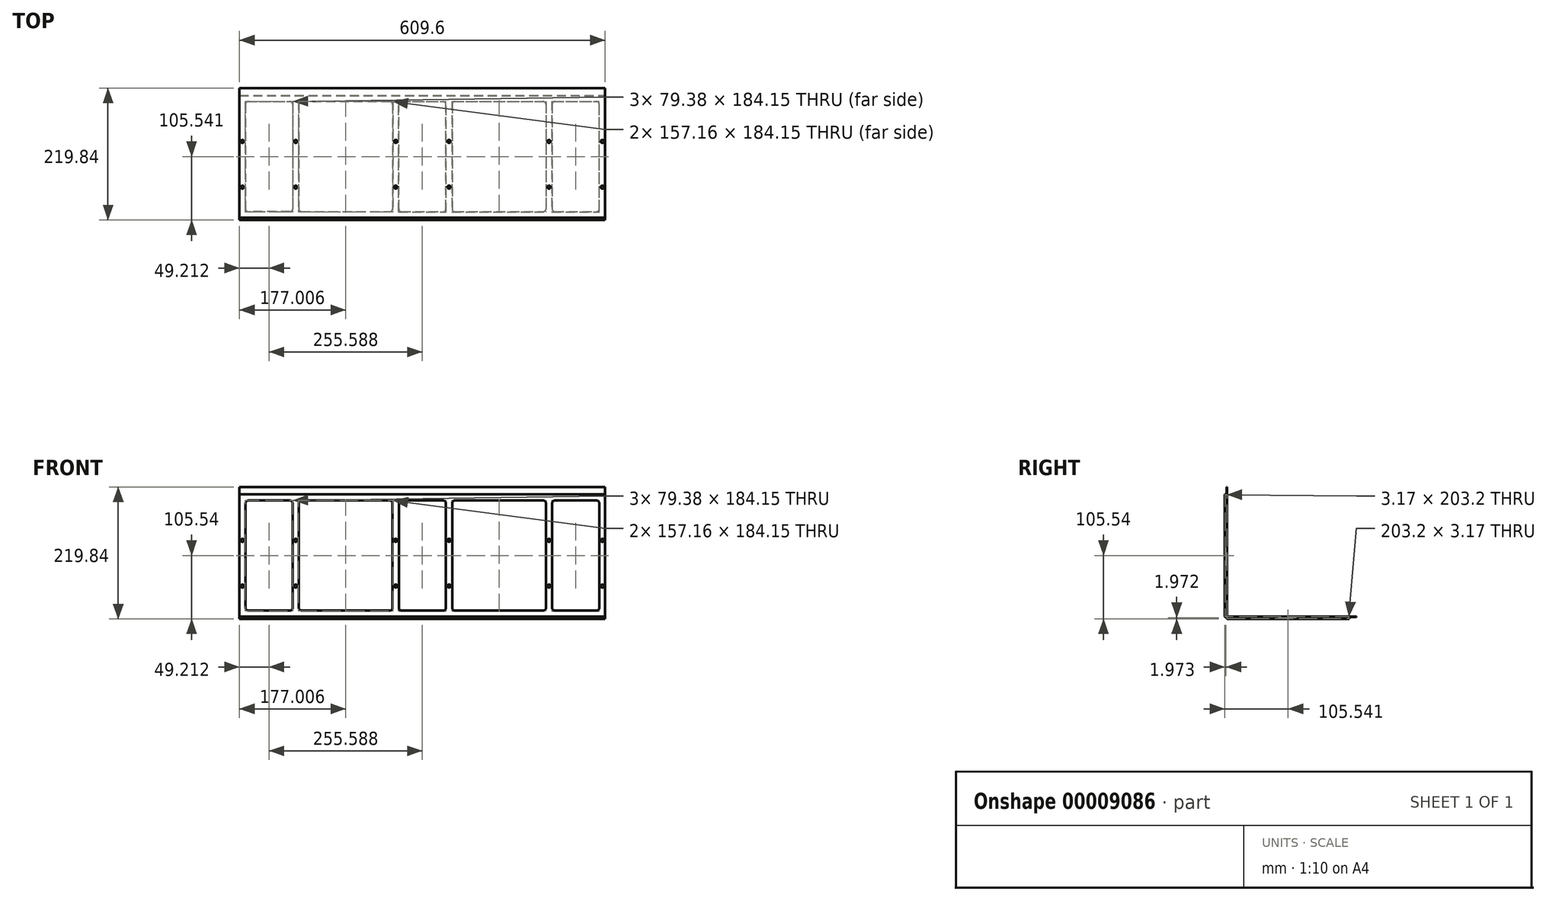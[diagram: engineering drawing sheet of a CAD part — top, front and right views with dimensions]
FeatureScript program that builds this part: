
annotation { "Feature Type Name" : "Feature", "Feature Type Description" : "" }
export const myFeature = defineFeature(function(context is Context, id is Id, definition is map)
    precondition{}
    {
        {
            var Q0;
            Q0=qCreatedBy(makeId("Front.planeOp"),FACE);
            var sketch = newSketch(context, id + "F0", { "sketchPlane" : qUnion([Q0])});
            skLineSegment(sketch, "E0.bottom", {"start": v(0, 0) * mm, "end": v(609.6, 0) * mm});
            skLineSegment(sketch, "E0.top", {"start": v(0, 203.2) * mm, "end": v(609.6, 203.2) * mm});
            skLineSegment(sketch, "E0.left", {"start": v(0, 0) * mm, "end": v(0, 203.2) * mm});
            skLineSegment(sketch, "E0.right", {"start": v(609.6, 0) * mm, "end": v(609.6, 203.2) * mm});
            skLineSegment(sketch, "E1.left", {"start": v(9.52, 193.68) * mm, "end": v(9.53, 9.52) * mm});
            skLineSegment(sketch, "E2.right", {"start": v(600.08, 9.53) * mm, "end": v(600.08, 193.68) * mm});
            skPoint(sketch, "E3", {"position": v(304.8, 203.2) * mm});
            skPoint(sketch, "E4", {"position": v(304.8, 0) * mm});
            skLineSegment(sketch, "E5.bottom", {"start": v(354.01, 193.68) * mm, "end": v(511.18, 193.68) * mm});
            skLineSegment(sketch, "E5.top", {"start": v(354.01, 9.53) * mm, "end": v(511.18, 9.53) * mm});
            skCircle(sketch, "E6", {"center": v(4.76, 127) * mm, "radius": 2.54 * mm});
            skCircle(sketch, "E7", {"center": v(4.76, 50.8) * mm, "radius": 2.54 * mm});
            skCircle(sketch, "E8", {"center": v(604.84, 127) * mm, "radius": 2.54 * mm});
            skCircle(sketch, "E9", {"center": v(604.84, 50.8) * mm, "radius": 2.54 * mm});
            skLineSegment(sketch, "E10.bottom", {"start": v(88.9, 193.68) * mm, "end": v(98.42, 193.68) * mm, "construction": true});
            skLineSegment(sketch, "E10.top", {"start": v(88.9, 9.52) * mm, "end": v(98.43, 9.52) * mm, "construction": true});
            skLineSegment(sketch, "E10.left", {"start": v(88.9, 193.68) * mm, "end": v(88.9, 9.53) * mm});
            skLineSegment(sketch, "E10.right", {"start": v(98.43, 193.68) * mm, "end": v(98.43, 9.53) * mm});
            skPoint(sketch, "E11", {"position": v(93.66, 193.68) * mm});
            skPoint(sketch, "E12", {"position": v(93.66, 127) * mm});
            skPoint(sketch, "E13", {"position": v(93.66, 50.8) * mm});
            skLineSegment(sketch, "E14", {"start": v(265.11, 9.53) * mm, "end": v(265.11, 193.68) * mm});
            skLineSegment(sketch, "E15", {"start": v(265.11, 193.68) * mm, "end": v(255.59, 193.68) * mm, "construction": true});
            skLineSegment(sketch, "E16", {"start": v(255.59, 193.68) * mm, "end": v(255.59, 9.53) * mm});
            skLineSegment(sketch, "E17", {"start": v(344.49, 9.53) * mm, "end": v(344.49, 193.67) * mm});
            skLineSegment(sketch, "E18", {"start": v(344.49, 193.68) * mm, "end": v(354.01, 193.68) * mm, "construction": true});
            skLineSegment(sketch, "E19", {"start": v(354.01, 193.68) * mm, "end": v(354.01, 9.53) * mm});
            skLineSegment(sketch, "E20.trimOffspring", {"start": v(265.11, 193.68) * mm, "end": v(344.49, 193.68) * mm});
            skPoint(sketch, "E21", {"position": v(260.35, 193.68) * mm});
            skPoint(sketch, "E22", {"position": v(349.25, 193.68) * mm});
            skCircle(sketch, "E23", {"center": v(93.66, 127) * mm, "radius": 2.54 * mm});
            skCircle(sketch, "E24", {"center": v(93.66, 50.8) * mm, "radius": 2.54 * mm});
            skCircle(sketch, "E25", {"center": v(260.35, 50.8) * mm, "radius": 2.54 * mm});
            skCircle(sketch, "E26", {"center": v(260.35, 127) * mm, "radius": 2.54 * mm});
            skCircle(sketch, "E27", {"center": v(349.25, 127) * mm, "radius": 2.54 * mm});
            skCircle(sketch, "E28", {"center": v(349.25, 50.8) * mm, "radius": 2.54 * mm});
            skLineSegment(sketch, "E29.trimOffspring", {"start": v(265.11, 9.53) * mm, "end": v(344.49, 9.53) * mm});
            skLineSegment(sketch, "E30.bottom", {"start": v(520.7, 193.68) * mm, "end": v(511.18, 193.68) * mm, "construction": true});
            skLineSegment(sketch, "E30.left", {"start": v(511.18, 193.68) * mm, "end": v(511.18, 9.53) * mm});
            skLineSegment(sketch, "E30.right", {"start": v(520.7, 193.68) * mm, "end": v(520.7, 9.53) * mm});
            skLineSegment(sketch, "E31.trimOffspring", {"start": v(520.7, 9.53) * mm, "end": v(600.08, 9.53) * mm});
            skLineSegment(sketch, "E32.trimOffspring", {"start": v(520.7, 193.68) * mm, "end": v(600.08, 193.68) * mm});
            skCircle(sketch, "E33", {"center": v(515.94, 127) * mm, "radius": 2.54 * mm});
            skCircle(sketch, "E34", {"center": v(515.94, 50.8) * mm, "radius": 2.54 * mm});
            skPoint(sketch, "E35", {"position": v(515.94, 193.67) * mm});
            skLineSegment(sketch, "E36", {"start": v(515.94, 193.67) * mm, "end": v(515.94, 9.53) * mm, "construction": true});
            skLineSegment(sketch, "E37", {"start": v(354.01, 9.53) * mm, "end": v(600.08, 9.53) * mm, "construction": true});
            skLineSegment(sketch, "E38", {"start": v(98.42, 193.68) * mm, "end": v(255.59, 193.68) * mm});
            skLineSegment(sketch, "E39", {"start": v(255.59, 9.53) * mm, "end": v(98.43, 9.52) * mm});
            skLineSegment(sketch, "E40", {"start": v(88.9, 9.53) * mm, "end": v(9.53, 9.52) * mm});
            skLineSegment(sketch, "E41", {"start": v(9.52, 193.68) * mm, "end": v(88.9, 193.68) * mm});
            skPoint(sketch, "E42", {"position": v(304.8, 9.53) * mm});
            skSolve(sketch);
        }
        {
            var Q0;
            Q0=makeQuery(id+"F0.imprint","IMPRINT",FACE,{"disambiguationData":[TD([[makeQuery(id+"F0.imprint","IMPRINT",EDGE,{"derivedFrom":sQuery(id+"F0.wireOp",EDGE,"E0.bottom")}),1.0]])]});
            extrude(context, id + "F1", {"entities" : qUnion([Q0]), "depth" : 3.17 * mm});
        }
        {
            var Q0;
            Q0=makeQuery(id+"F1.opExtrude","SWEPT_FACE",FACE,{"disambiguationData":[OSD([sQuery(id+"F0.wireOp",EDGE,"E0.right")])]});
            var sketch = newSketch(context, id + "F2", { "sketchPlane" : qUnion([Q0])});
            skLineSegment(sketch, "E43.0.0", {"start": v(0, 0) * mm, "end": v(0, 203.2) * mm});
            skLineSegment(sketch, "E43.0.1", {"start": v(0, 203.2) * mm, "end": v(-3.18, 203.2) * mm});
            skLineSegment(sketch, "E43.0.2", {"start": v(-3.18, 203.2) * mm, "end": v(-3.18, 0) * mm});
            skLineSegment(sketch, "E43.0.3", {"start": v(-3.18, 0) * mm, "end": v(0, 0) * mm});
            skLineSegment(sketch, "E44.0", {"start": v(0.38, 0) * mm, "end": v(0.38, 203.2) * mm});
            skLineSegment(sketch, "E45.0", {"start": v(-3.56, 203.2) * mm, "end": v(-3.56, 0) * mm});
            skLineSegment(sketch, "E46", {"start": v(-3.18, 203.2) * mm, "end": v(0, 203.2) * mm});
            skLineSegment(sketch, "E47", {"start": v(-3.56, 0) * mm, "end": v(0.38, 0) * mm});
            skLineSegment(sketch, "E48", {"start": v(0.38, 203.2) * mm, "end": v(0.38, 215.9) * mm});
            skLineSegment(sketch, "E49", {"start": v(0.38, 215.9) * mm, "end": v(-0.38, 215.9) * mm});
            skLineSegment(sketch, "E50", {"start": v(-0.38, 215.9) * mm, "end": v(-0.38, 204.85) * mm});
            skLineSegment(sketch, "E51", {"start": v(-3.56, 203.2) * mm, "end": v(-3.56, 203.58) * mm});
            skLineSegment(sketch, "E52", {"start": v(-3.56, 203.58) * mm, "end": v(-1.65, 203.58) * mm});
            skPoint(sketch, "E53.visualSharp", {"position": v(-0.38, 203.58) * mm});
            skArc(sketch, "E53.filletArc", {"start": v(-1.65, 203.58) * mm, "mid": v(-0.75, 203.95) * mm, "end": v(-0.38, 204.85) * mm});
            skLineSegment(sketch, "E54", {"start": v(0.38, 0) * mm, "end": v(-1.52, -1.9) * mm});
            skLineSegment(sketch, "E55", {"start": v(-3.56, 0) * mm, "end": v(-3.56, -0.38) * mm});
            skArc(sketch, "E56", {"start": v(-1.52, -1.9) * mm, "mid": v(-2.48, -1.07) * mm, "end": v(-3.56, -0.38) * mm});
            skLineSegment(sketch, "E57", {"start": v(-1.83, -1.6) * mm, "end": v(-1.52, -1.9) * mm, "construction": true});
            skSolve(sketch);
        }
        {
            var Q0;
            {var subQ2=sQuery(id+"F2.wireOp",EDGE,"E43.0.0");Q0=makeQuery(id+"F2.imprint","IMPRINT",FACE,{"disambiguationData":[TD([[makeQuery(id+"F2.imprint","IMPRINT",EDGE,{"derivedFrom":subQ2}),1.0]])]});}
            var Q1;
            {var subQ1=sQuery(id+"F2.wireOp",EDGE,"E54");Q1=makeQuery(id+"F2.imprint","IMPRINT",FACE,{"disambiguationData":[TD([[makeQuery(id+"F2.imprint","IMPRINT",EDGE,{"derivedFrom":subQ1}),-1.0]])]});}
            var Q2;
            {var subQ2=sQuery(id+"F2.wireOp",EDGE,"E43.0.0");Q2=makeQuery(id+"F2.imprint","IMPRINT",FACE,{"disambiguationData":[TD([[makeQuery(id+"F2.imprint","IMPRINT",EDGE,{"derivedFrom":subQ2}),-1.0]])]});}
            var Q3;
            Q3=makeQuery(id+"F1.opExtrude","SWEPT_FACE",FACE,{"disambiguationData":[OSD([sQuery(id+"F0.wireOp",EDGE,"E0.left")])]});
            extrude(context, id + "F3", {"entities" : qUnion([Q0, Q1, Q2]), "endBound" : BoundingType.UP_TO_SURFACE, "oppositeDirection" : true, "endBoundEntityFace" : qUnion([Q3]), "depth" : 25.4 * mm});
        }
        {
            var Q0;
            Q0=makeQuery(id+"F0.imprint","IMPRINT",FACE,{"disambiguationData":[TD([[makeQuery(id+"F0.imprint","IMPRINT",EDGE,{"derivedFrom":sQuery(id+"F0.wireOp",EDGE,"E0.bottom")}),1.0]])]});
            var Q1;
            Q1=makeQuery(id+"F0.imprint","IMPRINT",FACE,{"disambiguationData":[TD([[makeQuery(id+"F0.imprint","IMPRINT",EDGE,{"derivedFrom":sQuery(id+"F0.wireOp",EDGE,"e5c9517b-3403-446c-b804-9a1888062617")}),1.0]])]});
            var Q2;
            Q2=makeQuery(id+"F0.imprint","IMPRINT",FACE,{"disambiguationData":[TD([[makeQuery(id+"F0.imprint","IMPRINT",EDGE,{"derivedFrom":sQuery(id+"F0.wireOp",EDGE,"d61da92c-88b1-4440-b826-febfc96da58b")}),1.0]])]});
            var Q3;
            Q3=makeQuery(id+"F0.imprint","IMPRINT",FACE,{"disambiguationData":[TD([[makeQuery(id+"F0.imprint","IMPRINT",EDGE,{"derivedFrom":sQuery(id+"F0.wireOp",EDGE,"46ce25ad-17ab-4da1-9f69-b3d8d2fa4a44")}),1.0]])]});
            var Q4;
            Q4=makeQuery(id+"F0.imprint","IMPRINT",FACE,{"disambiguationData":[TD([[makeQuery(id+"F0.imprint","IMPRINT",EDGE,{"derivedFrom":sQuery(id+"F0.wireOp",EDGE,"ffe5e0e1-37b3-4eca-acac-06d890d8a48e")}),1.0]])]});
            var Q5;
            Q5=makeQuery(id+"F0.imprint","IMPRINT",FACE,{"disambiguationData":[TD([[makeQuery(id+"F0.imprint","IMPRINT",EDGE,{"derivedFrom":sQuery(id+"F0.wireOp",EDGE,"E9")}),1.0]])]});
            var Q6;
            Q6=makeQuery(id+"F0.imprint","IMPRINT",FACE,{"disambiguationData":[TD([[makeQuery(id+"F0.imprint","IMPRINT",EDGE,{"derivedFrom":sQuery(id+"F0.wireOp",EDGE,"E8")}),1.0]])]});
            var Q7;
            Q7=makeQuery(id+"F0.imprint","IMPRINT",FACE,{"disambiguationData":[TD([[makeQuery(id+"F0.imprint","IMPRINT",EDGE,{"derivedFrom":sQuery(id+"F0.wireOp",EDGE,"8ca14061-9922-471c-a98a-c78a47010712")}),1.0]])]});
            var Q8;
            Q8=makeQuery(id+"F0.imprint","IMPRINT",FACE,{"disambiguationData":[TD([[makeQuery(id+"F0.imprint","IMPRINT",EDGE,{"derivedFrom":sQuery(id+"F0.wireOp",EDGE,"fd383d34-7c74-4bab-aac5-eb13519cfafe")}),1.0]])]});
            var Q9;
            Q9=makeQuery(id+"F0.imprint","IMPRINT",FACE,{"disambiguationData":[TD([[makeQuery(id+"F0.imprint","IMPRINT",EDGE,{"derivedFrom":sQuery(id+"F0.wireOp",EDGE,"E7")}),1.0]])]});
            var Q10;
            Q10=makeQuery(id+"F0.imprint","IMPRINT",FACE,{"disambiguationData":[TD([[makeQuery(id+"F0.imprint","IMPRINT",EDGE,{"derivedFrom":sQuery(id+"F0.wireOp",EDGE,"E6")}),1.0]])]});
            var Q11;
            Q11=makeQuery(id+"F3.opExtrude","SWEPT_FACE",FACE,{"disambiguationData":[OSD([sQuery(id+"F2.wireOp",EDGE,"E45.0"),sQuery(id+"F2.wireOp",EDGE,"E51"),sQuery(id+"F2.wireOp",EDGE,"E55")])]});
            extrude(context, id + "F4", {"entities" : qUnion([Q0, Q1, Q2, Q3, Q4, Q5, Q6, Q7, Q8, Q9, Q10, Q11]), "operationType" : NewBodyOperationType.REMOVE, "depth" : 3.17 * mm});
        }
        {
            var Q0;
            Q0=makeQuery(id+"F0.imprint","IMPRINT",FACE,{"disambiguationData":[TD([[makeQuery(id+"F0.imprint","IMPRINT",EDGE,{"derivedFrom":sQuery(id+"F0.wireOp",EDGE,"8ca14061-9922-471c-a98a-c78a47010712")}),1.0]])]});
            var Q1;
            Q1=makeQuery(id+"F0.imprint","IMPRINT",FACE,{"disambiguationData":[TD([[makeQuery(id+"F0.imprint","IMPRINT",EDGE,{"derivedFrom":sQuery(id+"F0.wireOp",EDGE,"fd383d34-7c74-4bab-aac5-eb13519cfafe")}),1.0]])]});
            var Q2;
            Q2=makeQuery(id+"F0.imprint","IMPRINT",FACE,{"disambiguationData":[TD([[makeQuery(id+"F0.imprint","IMPRINT",EDGE,{"derivedFrom":sQuery(id+"F0.wireOp",EDGE,"E7")}),1.0]])]});
            var Q3;
            Q3=makeQuery(id+"F0.imprint","IMPRINT",FACE,{"disambiguationData":[TD([[makeQuery(id+"F0.imprint","IMPRINT",EDGE,{"derivedFrom":sQuery(id+"F0.wireOp",EDGE,"E6")}),1.0]])]});
            var Q4;
            Q4=makeQuery(id+"F0.imprint","IMPRINT",FACE,{"disambiguationData":[TD([[makeQuery(id+"F0.imprint","IMPRINT",EDGE,{"derivedFrom":sQuery(id+"F0.wireOp",EDGE,"d61da92c-88b1-4440-b826-febfc96da58b")}),1.0]])]});
            var Q5;
            Q5=makeQuery(id+"F0.imprint","IMPRINT",FACE,{"disambiguationData":[TD([[makeQuery(id+"F0.imprint","IMPRINT",EDGE,{"derivedFrom":sQuery(id+"F0.wireOp",EDGE,"e5c9517b-3403-446c-b804-9a1888062617")}),1.0]])]});
            var Q6;
            Q6=makeQuery(id+"F0.imprint","IMPRINT",FACE,{"disambiguationData":[TD([[makeQuery(id+"F0.imprint","IMPRINT",EDGE,{"derivedFrom":sQuery(id+"F0.wireOp",EDGE,"ffe5e0e1-37b3-4eca-acac-06d890d8a48e")}),1.0]])]});
            var Q7;
            Q7=makeQuery(id+"F0.imprint","IMPRINT",FACE,{"disambiguationData":[TD([[makeQuery(id+"F0.imprint","IMPRINT",EDGE,{"derivedFrom":sQuery(id+"F0.wireOp",EDGE,"46ce25ad-17ab-4da1-9f69-b3d8d2fa4a44")}),1.0]])]});
            var Q8;
            Q8=makeQuery(id+"F0.imprint","IMPRINT",FACE,{"disambiguationData":[TD([[makeQuery(id+"F0.imprint","IMPRINT",EDGE,{"derivedFrom":sQuery(id+"F0.wireOp",EDGE,"E9")}),1.0]])]});
            var Q9;
            Q9=makeQuery(id+"F0.imprint","IMPRINT",FACE,{"disambiguationData":[TD([[makeQuery(id+"F0.imprint","IMPRINT",EDGE,{"derivedFrom":sQuery(id+"F0.wireOp",EDGE,"E8")}),1.0]])]});
            var Q10;
            Q10=makeQuery(id+"F0.imprint","IMPRINT",FACE,{"disambiguationData":[TD([[makeQuery(id+"F0.imprint","IMPRINT",EDGE,{"derivedFrom":sQuery(id+"F0.wireOp",EDGE,"E26")}),1.0]])]});
            var Q11;
            Q11=makeQuery(id+"F0.imprint","IMPRINT",FACE,{"disambiguationData":[TD([[makeQuery(id+"F0.imprint","IMPRINT",EDGE,{"derivedFrom":sQuery(id+"F0.wireOp",EDGE,"E25")}),1.0]])]});
            var Q12;
            Q12=makeQuery(id+"F0.imprint","IMPRINT",FACE,{"disambiguationData":[TD([[makeQuery(id+"F0.imprint","IMPRINT",EDGE,{"derivedFrom":sQuery(id+"F0.wireOp",EDGE,"E24")}),1.0]])]});
            var Q13;
            Q13=makeQuery(id+"F0.imprint","IMPRINT",FACE,{"disambiguationData":[TD([[makeQuery(id+"F0.imprint","IMPRINT",EDGE,{"derivedFrom":sQuery(id+"F0.wireOp",EDGE,"E23")}),1.0]])]});
            var Q14;
            Q14=makeQuery(id+"F0.imprint","IMPRINT",FACE,{"disambiguationData":[TD([[makeQuery(id+"F0.imprint","IMPRINT",EDGE,{"derivedFrom":sQuery(id+"F0.wireOp",EDGE,"E28")}),1.0]])]});
            var Q15;
            Q15=makeQuery(id+"F0.imprint","IMPRINT",FACE,{"disambiguationData":[TD([[makeQuery(id+"F0.imprint","IMPRINT",EDGE,{"derivedFrom":sQuery(id+"F0.wireOp",EDGE,"E27")}),1.0]])]});
            var Q16;
            Q16=makeQuery(id+"F0.imprint","IMPRINT",FACE,{"disambiguationData":[TD([[makeQuery(id+"F0.imprint","IMPRINT",EDGE,{"derivedFrom":sQuery(id+"F0.wireOp",EDGE,"E34")}),1.0]])]});
            var Q17;
            Q17=makeQuery(id+"F0.imprint","IMPRINT",FACE,{"disambiguationData":[TD([[makeQuery(id+"F0.imprint","IMPRINT",EDGE,{"derivedFrom":sQuery(id+"F0.wireOp",EDGE,"E33")}),1.0]])]});
            extrude(context, id + "F5", {"entities" : qUnion([Q0, Q1, Q2, Q3, Q4, Q5, Q6, Q7, Q8, Q9, Q10, Q11, Q12, Q13, Q14, Q15, Q16, Q17]), "operationType" : NewBodyOperationType.REMOVE, "endBound" : BoundingType.SYMMETRIC, "depth" : 25.4 * mm});
        }
        {
            var Q0;
            Q0=makeQuery(id+"F3.opExtrude","SWEPT_FACE",FACE,{"disambiguationData":[OSD([sQuery(id+"F2.wireOp",EDGE,"E45.0"),sQuery(id+"F2.wireOp",EDGE,"E51"),sQuery(id+"F2.wireOp",EDGE,"E55")])]});
            var sketch = newSketch(context, id + "F6", { "sketchPlane" : qUnion([Q0])});
            skLineSegment(sketch, "E58.0.1", {"start": v(0, 0) * mm, "end": v(609.6, 0) * mm});
            skLineSegment(sketch, "E58.0.3", {"start": v(609.6, 203.2) * mm, "end": v(0, 203.2) * mm});
            skLineSegment(sketch, "E59.0.0", {"start": v(255.59, 193.68) * mm, "end": v(98.42, 193.68) * mm});
            skLineSegment(sketch, "E59.0.2", {"start": v(98.43, 9.52) * mm, "end": v(255.59, 9.53) * mm});
            skLineSegment(sketch, "E60.1", {"start": v(609.6, 0) * mm, "end": v(609.6, -3.18) * mm});
            skLineSegment(sketch, "E60.3", {"start": v(609.6, -3.18) * mm, "end": v(609.6, 0) * mm});
            skLineSegment(sketch, "E60.6", {"start": v(609.6, -3.18) * mm, "end": v(609.6, 0) * mm});
            skLineSegment(sketch, "E60.7", {"start": v(609.6, -3.56) * mm, "end": v(609.6, 0.38) * mm});
            skLineSegment(sketch, "E60.9", {"start": v(609.6, 0.38) * mm, "end": v(609.6, -0.38) * mm});
            skLineSegment(sketch, "E60.12", {"start": v(609.6, -3.56) * mm, "end": v(609.6, -1.65) * mm});
            skPoint(sketch, "E60.13", {"position": v(609.6, 203.58) * mm});
            skLineSegment(sketch, "E60.14", {"start": v(609.6, 204.85) * mm, "end": v(609.6, 203.58) * mm});
            skLineSegment(sketch, "E60.15", {"start": v(609.6, 0) * mm, "end": v(609.6, -1.9) * mm});
            skLineSegment(sketch, "E60.17", {"start": v(609.6, -0.38) * mm, "end": v(609.6, -1.9) * mm});
            skLineSegment(sketch, "E60.18", {"start": v(609.6, -1.6) * mm, "end": v(609.6, -1.9) * mm});
            skLineSegment(sketch, "E61.0", {"start": v(88.9, 193.68) * mm, "end": v(88.9, 9.53) * mm});
            skLineSegment(sketch, "E61.1", {"start": v(88.9, 9.53) * mm, "end": v(9.53, 9.52) * mm});
            skLineSegment(sketch, "E61.2", {"start": v(9.52, 193.68) * mm, "end": v(88.9, 193.68) * mm});
            skLineSegment(sketch, "E61.3", {"start": v(9.52, 193.68) * mm, "end": v(9.53, 9.52) * mm});
            skLineSegment(sketch, "E62.0", {"start": v(98.43, 193.68) * mm, "end": v(98.43, 9.53) * mm});
            skLineSegment(sketch, "E62.1", {"start": v(255.59, 193.68) * mm, "end": v(255.59, 9.53) * mm});
            skLineSegment(sketch, "E62.2", {"start": v(265.11, 9.53) * mm, "end": v(265.11, 193.68) * mm});
            skLineSegment(sketch, "E62.3", {"start": v(344.49, 9.53) * mm, "end": v(344.49, 193.67) * mm});
            skLineSegment(sketch, "E62.4", {"start": v(354.01, 193.68) * mm, "end": v(354.01, 9.53) * mm});
            skLineSegment(sketch, "E62.5", {"start": v(511.18, 193.68) * mm, "end": v(511.18, 9.53) * mm});
            skLineSegment(sketch, "E62.6", {"start": v(520.7, 193.68) * mm, "end": v(520.7, 9.53) * mm});
            skLineSegment(sketch, "E62.7", {"start": v(600.08, 9.53) * mm, "end": v(600.08, 193.68) * mm});
            skLineSegment(sketch, "E62.8", {"start": v(354.01, 193.68) * mm, "end": v(511.18, 193.68) * mm});
            skLineSegment(sketch, "E62.9", {"start": v(520.7, 193.68) * mm, "end": v(600.08, 193.68) * mm});
            skLineSegment(sketch, "E62.10", {"start": v(520.7, 9.53) * mm, "end": v(600.08, 9.53) * mm});
            skLineSegment(sketch, "E62.11", {"start": v(354.01, 9.53) * mm, "end": v(511.18, 9.53) * mm});
            skLineSegment(sketch, "E62.12", {"start": v(265.11, 193.68) * mm, "end": v(344.49, 193.68) * mm});
            skLineSegment(sketch, "E62.13", {"start": v(265.11, 9.53) * mm, "end": v(344.49, 9.53) * mm});
            skLineSegment(sketch, "E63.0", {"start": v(9.9, 193.3) * mm, "end": v(88.52, 193.3) * mm});
            skLineSegment(sketch, "E63.1", {"start": v(9.9, 193.3) * mm, "end": v(9.9, 9.9) * mm});
            skLineSegment(sketch, "E63.2", {"start": v(88.52, 9.9) * mm, "end": v(9.9, 9.9) * mm});
            skLineSegment(sketch, "E63.3", {"start": v(88.52, 193.3) * mm, "end": v(88.52, 9.9) * mm});
            skLineSegment(sketch, "E64.0", {"start": v(255.2, 193.3) * mm, "end": v(98.8, 193.3) * mm});
            skLineSegment(sketch, "E64.1", {"start": v(255.2, 193.3) * mm, "end": v(255.2, 9.9) * mm});
            skLineSegment(sketch, "E64.2", {"start": v(98.8, 9.9) * mm, "end": v(255.2, 9.9) * mm});
            skLineSegment(sketch, "E64.3", {"start": v(98.8, 193.3) * mm, "end": v(98.8, 9.9) * mm});
            skLineSegment(sketch, "E65.0", {"start": v(265.5, 193.3) * mm, "end": v(344.1, 193.3) * mm});
            skLineSegment(sketch, "E65.1", {"start": v(265.5, 9.9) * mm, "end": v(265.5, 193.3) * mm});
            skLineSegment(sketch, "E65.2", {"start": v(265.5, 9.9) * mm, "end": v(344.1, 9.9) * mm});
            skLineSegment(sketch, "E65.3", {"start": v(344.1, 9.9) * mm, "end": v(344.1, 193.3) * mm});
            skLineSegment(sketch, "E66.0", {"start": v(354.4, 193.3) * mm, "end": v(510.8, 193.3) * mm});
            skLineSegment(sketch, "E66.1", {"start": v(354.4, 193.3) * mm, "end": v(354.4, 9.9) * mm});
            skLineSegment(sketch, "E66.2", {"start": v(354.4, 9.9) * mm, "end": v(510.8, 9.9) * mm});
            skLineSegment(sketch, "E66.3", {"start": v(510.8, 193.3) * mm, "end": v(510.8, 9.9) * mm});
            skLineSegment(sketch, "E67.0", {"start": v(521.08, 193.3) * mm, "end": v(599.7, 193.3) * mm});
            skLineSegment(sketch, "E67.1", {"start": v(521.08, 193.3) * mm, "end": v(521.08, 9.9) * mm});
            skLineSegment(sketch, "E67.2", {"start": v(521.08, 9.9) * mm, "end": v(599.7, 9.9) * mm});
            skLineSegment(sketch, "E67.3", {"start": v(599.7, 9.9) * mm, "end": v(599.7, 193.3) * mm});
            skSolve(sketch);
        }
        {
            var Q0;
            Q0=makeQuery(id+"F6.imprint","IMPRINT",FACE,{"disambiguationData":[TD([[makeQuery(id+"F6.imprint","IMPRINT",EDGE,{"derivedFrom":sQuery(id+"F6.wireOp",EDGE,"E66.0")}),-1.0]])]});
            var Q1;
            Q1=makeQuery(id+"F6.imprint","IMPRINT",FACE,{"disambiguationData":[TD([[makeQuery(id+"F6.imprint","IMPRINT",EDGE,{"derivedFrom":sQuery(id+"F6.wireOp",EDGE,"E65.0")}),-1.0]])]});
            var Q2;
            Q2=makeQuery(id+"F6.imprint","IMPRINT",FACE,{"disambiguationData":[TD([[makeQuery(id+"F6.imprint","IMPRINT",EDGE,{"derivedFrom":sQuery(id+"F6.wireOp",EDGE,"E64.0")}),1.0]])]});
            var Q3;
            Q3=makeQuery(id+"F6.imprint","IMPRINT",FACE,{"disambiguationData":[TD([[makeQuery(id+"F6.imprint","IMPRINT",EDGE,{"derivedFrom":sQuery(id+"F6.wireOp",EDGE,"E63.0")}),-1.0]])]});
            var Q4;
            Q4=makeQuery(id+"F6.imprint","IMPRINT",FACE,{"disambiguationData":[TD([[makeQuery(id+"F6.imprint","IMPRINT",EDGE,{"derivedFrom":sQuery(id+"F6.wireOp",EDGE,"E67.0")}),-1.0]])]});
            extrude(context, id + "F7", {"entities" : qUnion([Q0, Q1, Q2, Q3, Q4]), "operationType" : NewBodyOperationType.REMOVE, "oppositeDirection" : true, "depth" : 3.17 * mm});
        }
        {
            var Q0;
            Q0=makeQuery(id+"F7.boolean.opBoolean","COPY",FACE,{"derivedFrom":makeQuery(id+"F7.opExtrude","CAP_FACE",FACE,{"disambiguationData":[OSD([sQuery(id+"F6.wireOp",EDGE,"E67.0"),sQuery(id+"F6.wireOp",EDGE,"E67.1"),sQuery(id+"F6.wireOp",EDGE,"E67.2"),sQuery(id+"F6.wireOp",EDGE,"E67.3")])],"isStart":false})});
            var Q1;
            Q1=makeQuery(id+"F7.boolean.opBoolean","COPY",FACE,{"derivedFrom":makeQuery(id+"F7.opExtrude","CAP_FACE",FACE,{"disambiguationData":[OSD([sQuery(id+"F6.wireOp",EDGE,"E66.0"),sQuery(id+"F6.wireOp",EDGE,"E66.1"),sQuery(id+"F6.wireOp",EDGE,"E66.2"),sQuery(id+"F6.wireOp",EDGE,"E66.3")])],"isStart":false})});
            var Q2;
            Q2=makeQuery(id+"F7.boolean.opBoolean","COPY",FACE,{"derivedFrom":makeQuery(id+"F7.opExtrude","CAP_FACE",FACE,{"disambiguationData":[OSD([sQuery(id+"F6.wireOp",EDGE,"E65.0"),sQuery(id+"F6.wireOp",EDGE,"E65.1"),sQuery(id+"F6.wireOp",EDGE,"E65.2"),sQuery(id+"F6.wireOp",EDGE,"E65.3")])],"isStart":false})});
            var Q3;
            Q3=makeQuery(id+"F7.boolean.opBoolean","COPY",FACE,{"derivedFrom":makeQuery(id+"F7.opExtrude","CAP_FACE",FACE,{"disambiguationData":[OSD([sQuery(id+"F6.wireOp",EDGE,"E64.0"),sQuery(id+"F6.wireOp",EDGE,"E64.1"),sQuery(id+"F6.wireOp",EDGE,"E64.2"),sQuery(id+"F6.wireOp",EDGE,"E64.3")])],"isStart":false})});
            var Q4;
            Q4=makeQuery(id+"F7.boolean.opBoolean","COPY",FACE,{"derivedFrom":makeQuery(id+"F7.opExtrude","CAP_FACE",FACE,{"disambiguationData":[OSD([sQuery(id+"F6.wireOp",EDGE,"E63.0"),sQuery(id+"F6.wireOp",EDGE,"E63.1"),sQuery(id+"F6.wireOp",EDGE,"E63.2"),sQuery(id+"F6.wireOp",EDGE,"E63.3")])],"isStart":false})});
            fillet(context, id + "F8", {"entities" : qUnion([Q0, Q1, Q2, Q3, Q4]), "radius" : 5.08 * mm, "tangentPropagation" : true, "allowEdgeOverflow" : false});
        }
        {
            var Q0;
            Q0=makeQuery(id+"F8.opFillet","BLEND_EDGE",EDGE,{"blendedFrom":[makeQuery(id+"F7.boolean.opBoolean","COPY",EDGE,{"derivedFrom":makeQuery(id+"F7.opExtrude","CAP_EDGE",EDGE,{"disambiguationData":[OSD([sQuery(id+"F6.wireOp",EDGE,"E63.1")])],"isStart":false})}),makeQuery(id+"F7.boolean.opBoolean","COPY",EDGE,{"derivedFrom":makeQuery(id+"F7.opExtrude","CAP_EDGE",EDGE,{"disambiguationData":[OSD([sQuery(id+"F6.wireOp",EDGE,"E63.2")])],"isStart":false})})],"blendedInto":[]});
            var Q1;
            Q1=makeQuery(id+"F8.opFillet","BLEND_EDGE",EDGE,{"blendedFrom":[makeQuery(id+"F7.boolean.opBoolean","COPY",EDGE,{"derivedFrom":makeQuery(id+"F7.opExtrude","CAP_EDGE",EDGE,{"disambiguationData":[OSD([sQuery(id+"F6.wireOp",EDGE,"E63.0")])],"isStart":false})}),makeQuery(id+"F7.boolean.opBoolean","COPY",EDGE,{"derivedFrom":makeQuery(id+"F7.opExtrude","CAP_EDGE",EDGE,{"disambiguationData":[OSD([sQuery(id+"F6.wireOp",EDGE,"E63.1")])],"isStart":false})})],"blendedInto":[]});
            var Q2;
            Q2=makeQuery(id+"F8.opFillet","BLEND_EDGE",EDGE,{"blendedFrom":[makeQuery(id+"F7.boolean.opBoolean","COPY",EDGE,{"derivedFrom":makeQuery(id+"F7.opExtrude","CAP_EDGE",EDGE,{"disambiguationData":[OSD([sQuery(id+"F6.wireOp",EDGE,"E63.0")])],"isStart":false})}),makeQuery(id+"F7.boolean.opBoolean","COPY",EDGE,{"derivedFrom":makeQuery(id+"F7.opExtrude","CAP_EDGE",EDGE,{"disambiguationData":[OSD([sQuery(id+"F6.wireOp",EDGE,"E63.3")])],"isStart":false})})],"blendedInto":[]});
            var Q3;
            Q3=makeQuery(id+"F8.opFillet","BLEND_EDGE",EDGE,{"blendedFrom":[makeQuery(id+"F7.boolean.opBoolean","COPY",EDGE,{"derivedFrom":makeQuery(id+"F7.opExtrude","CAP_EDGE",EDGE,{"disambiguationData":[OSD([sQuery(id+"F6.wireOp",EDGE,"E63.2")])],"isStart":false})}),makeQuery(id+"F7.boolean.opBoolean","COPY",EDGE,{"derivedFrom":makeQuery(id+"F7.opExtrude","CAP_EDGE",EDGE,{"disambiguationData":[OSD([sQuery(id+"F6.wireOp",EDGE,"E63.3")])],"isStart":false})})],"blendedInto":[]});
            var Q4;
            Q4=makeQuery(id+"F8.opFillet","BLEND_EDGE",EDGE,{"blendedFrom":[makeQuery(id+"F7.boolean.opBoolean","COPY",EDGE,{"derivedFrom":makeQuery(id+"F7.opExtrude","CAP_EDGE",EDGE,{"disambiguationData":[OSD([sQuery(id+"F6.wireOp",EDGE,"E64.1")])],"isStart":false})}),makeQuery(id+"F7.boolean.opBoolean","COPY",EDGE,{"derivedFrom":makeQuery(id+"F7.opExtrude","CAP_EDGE",EDGE,{"disambiguationData":[OSD([sQuery(id+"F6.wireOp",EDGE,"E64.2")])],"isStart":false})})],"blendedInto":[]});
            var Q5;
            Q5=makeQuery(id+"F8.opFillet","BLEND_EDGE",EDGE,{"blendedFrom":[makeQuery(id+"F7.boolean.opBoolean","COPY",EDGE,{"derivedFrom":makeQuery(id+"F7.opExtrude","CAP_EDGE",EDGE,{"disambiguationData":[OSD([sQuery(id+"F6.wireOp",EDGE,"E64.0")])],"isStart":false})}),makeQuery(id+"F7.boolean.opBoolean","COPY",EDGE,{"derivedFrom":makeQuery(id+"F7.opExtrude","CAP_EDGE",EDGE,{"disambiguationData":[OSD([sQuery(id+"F6.wireOp",EDGE,"E64.1")])],"isStart":false})})],"blendedInto":[]});
            var Q6;
            Q6=makeQuery(id+"F8.opFillet","BLEND_EDGE",EDGE,{"blendedFrom":[makeQuery(id+"F7.boolean.opBoolean","COPY",EDGE,{"derivedFrom":makeQuery(id+"F7.opExtrude","CAP_EDGE",EDGE,{"disambiguationData":[OSD([sQuery(id+"F6.wireOp",EDGE,"E65.0")])],"isStart":false})}),makeQuery(id+"F7.boolean.opBoolean","COPY",EDGE,{"derivedFrom":makeQuery(id+"F7.opExtrude","CAP_EDGE",EDGE,{"disambiguationData":[OSD([sQuery(id+"F6.wireOp",EDGE,"E65.3")])],"isStart":false})})],"blendedInto":[]});
            var Q7;
            Q7=makeQuery(id+"F8.opFillet","BLEND_EDGE",EDGE,{"blendedFrom":[makeQuery(id+"F7.boolean.opBoolean","COPY",EDGE,{"derivedFrom":makeQuery(id+"F7.opExtrude","CAP_EDGE",EDGE,{"disambiguationData":[OSD([sQuery(id+"F6.wireOp",EDGE,"E65.2")])],"isStart":false})}),makeQuery(id+"F7.boolean.opBoolean","COPY",EDGE,{"derivedFrom":makeQuery(id+"F7.opExtrude","CAP_EDGE",EDGE,{"disambiguationData":[OSD([sQuery(id+"F6.wireOp",EDGE,"E65.3")])],"isStart":false})})],"blendedInto":[]});
            var Q8;
            Q8=makeQuery(id+"F8.opFillet","BLEND_EDGE",EDGE,{"blendedFrom":[makeQuery(id+"F7.boolean.opBoolean","COPY",EDGE,{"derivedFrom":makeQuery(id+"F7.opExtrude","CAP_EDGE",EDGE,{"disambiguationData":[OSD([sQuery(id+"F6.wireOp",EDGE,"E66.0")])],"isStart":false})}),makeQuery(id+"F7.boolean.opBoolean","COPY",EDGE,{"derivedFrom":makeQuery(id+"F7.opExtrude","CAP_EDGE",EDGE,{"disambiguationData":[OSD([sQuery(id+"F6.wireOp",EDGE,"E66.3")])],"isStart":false})})],"blendedInto":[]});
            var Q9;
            Q9=makeQuery(id+"F8.opFillet","BLEND_EDGE",EDGE,{"blendedFrom":[makeQuery(id+"F7.boolean.opBoolean","COPY",EDGE,{"derivedFrom":makeQuery(id+"F7.opExtrude","CAP_EDGE",EDGE,{"disambiguationData":[OSD([sQuery(id+"F6.wireOp",EDGE,"E66.2")])],"isStart":false})}),makeQuery(id+"F7.boolean.opBoolean","COPY",EDGE,{"derivedFrom":makeQuery(id+"F7.opExtrude","CAP_EDGE",EDGE,{"disambiguationData":[OSD([sQuery(id+"F6.wireOp",EDGE,"E66.3")])],"isStart":false})})],"blendedInto":[]});
            var Q10;
            Q10=makeQuery(id+"F8.opFillet","BLEND_EDGE",EDGE,{"blendedFrom":[makeQuery(id+"F7.boolean.opBoolean","COPY",EDGE,{"derivedFrom":makeQuery(id+"F7.opExtrude","CAP_EDGE",EDGE,{"disambiguationData":[OSD([sQuery(id+"F6.wireOp",EDGE,"E67.0")])],"isStart":false})}),makeQuery(id+"F7.boolean.opBoolean","COPY",EDGE,{"derivedFrom":makeQuery(id+"F7.opExtrude","CAP_EDGE",EDGE,{"disambiguationData":[OSD([sQuery(id+"F6.wireOp",EDGE,"E67.3")])],"isStart":false})})],"blendedInto":[]});
            var Q11;
            Q11=makeQuery(id+"F8.opFillet","BLEND_EDGE",EDGE,{"blendedFrom":[makeQuery(id+"F7.boolean.opBoolean","COPY",EDGE,{"derivedFrom":makeQuery(id+"F7.opExtrude","CAP_EDGE",EDGE,{"disambiguationData":[OSD([sQuery(id+"F6.wireOp",EDGE,"E67.2")])],"isStart":false})}),makeQuery(id+"F7.boolean.opBoolean","COPY",EDGE,{"derivedFrom":makeQuery(id+"F7.opExtrude","CAP_EDGE",EDGE,{"disambiguationData":[OSD([sQuery(id+"F6.wireOp",EDGE,"E67.3")])],"isStart":false})})],"blendedInto":[]});
            var Q12;
            Q12=makeQuery(id+"F8.opFillet","BLEND_EDGE",EDGE,{"blendedFrom":[makeQuery(id+"F7.boolean.opBoolean","COPY",EDGE,{"derivedFrom":makeQuery(id+"F7.opExtrude","CAP_EDGE",EDGE,{"disambiguationData":[OSD([sQuery(id+"F6.wireOp",EDGE,"E67.0")])],"isStart":false})}),makeQuery(id+"F7.boolean.opBoolean","COPY",EDGE,{"derivedFrom":makeQuery(id+"F7.opExtrude","CAP_EDGE",EDGE,{"disambiguationData":[OSD([sQuery(id+"F6.wireOp",EDGE,"E67.1")])],"isStart":false})})],"blendedInto":[]});
            var Q13;
            Q13=makeQuery(id+"F8.opFillet","BLEND_EDGE",EDGE,{"blendedFrom":[makeQuery(id+"F7.boolean.opBoolean","COPY",EDGE,{"derivedFrom":makeQuery(id+"F7.opExtrude","CAP_EDGE",EDGE,{"disambiguationData":[OSD([sQuery(id+"F6.wireOp",EDGE,"E67.1")])],"isStart":false})}),makeQuery(id+"F7.boolean.opBoolean","COPY",EDGE,{"derivedFrom":makeQuery(id+"F7.opExtrude","CAP_EDGE",EDGE,{"disambiguationData":[OSD([sQuery(id+"F6.wireOp",EDGE,"E67.2")])],"isStart":false})})],"blendedInto":[]});
            var Q14;
            Q14=makeQuery(id+"F8.opFillet","BLEND_EDGE",EDGE,{"blendedFrom":[makeQuery(id+"F7.boolean.opBoolean","COPY",EDGE,{"derivedFrom":makeQuery(id+"F7.opExtrude","CAP_EDGE",EDGE,{"disambiguationData":[OSD([sQuery(id+"F6.wireOp",EDGE,"E66.1")])],"isStart":false})}),makeQuery(id+"F7.boolean.opBoolean","COPY",EDGE,{"derivedFrom":makeQuery(id+"F7.opExtrude","CAP_EDGE",EDGE,{"disambiguationData":[OSD([sQuery(id+"F6.wireOp",EDGE,"E66.2")])],"isStart":false})})],"blendedInto":[]});
            var Q15;
            Q15=makeQuery(id+"F8.opFillet","BLEND_EDGE",EDGE,{"blendedFrom":[makeQuery(id+"F7.boolean.opBoolean","COPY",EDGE,{"derivedFrom":makeQuery(id+"F7.opExtrude","CAP_EDGE",EDGE,{"disambiguationData":[OSD([sQuery(id+"F6.wireOp",EDGE,"E66.0")])],"isStart":false})}),makeQuery(id+"F7.boolean.opBoolean","COPY",EDGE,{"derivedFrom":makeQuery(id+"F7.opExtrude","CAP_EDGE",EDGE,{"disambiguationData":[OSD([sQuery(id+"F6.wireOp",EDGE,"E66.1")])],"isStart":false})})],"blendedInto":[]});
            var Q16;
            Q16=makeQuery(id+"F8.opFillet","BLEND_EDGE",EDGE,{"blendedFrom":[makeQuery(id+"F7.boolean.opBoolean","COPY",EDGE,{"derivedFrom":makeQuery(id+"F7.opExtrude","CAP_EDGE",EDGE,{"disambiguationData":[OSD([sQuery(id+"F6.wireOp",EDGE,"E65.0")])],"isStart":false})}),makeQuery(id+"F7.boolean.opBoolean","COPY",EDGE,{"derivedFrom":makeQuery(id+"F7.opExtrude","CAP_EDGE",EDGE,{"disambiguationData":[OSD([sQuery(id+"F6.wireOp",EDGE,"E65.1")])],"isStart":false})})],"blendedInto":[]});
            var Q17;
            Q17=makeQuery(id+"F8.opFillet","BLEND_EDGE",EDGE,{"blendedFrom":[makeQuery(id+"F7.boolean.opBoolean","COPY",EDGE,{"derivedFrom":makeQuery(id+"F7.opExtrude","CAP_EDGE",EDGE,{"disambiguationData":[OSD([sQuery(id+"F6.wireOp",EDGE,"E65.1")])],"isStart":false})}),makeQuery(id+"F7.boolean.opBoolean","COPY",EDGE,{"derivedFrom":makeQuery(id+"F7.opExtrude","CAP_EDGE",EDGE,{"disambiguationData":[OSD([sQuery(id+"F6.wireOp",EDGE,"E65.2")])],"isStart":false})})],"blendedInto":[]});
            var Q18;
            Q18=makeQuery(id+"F8.opFillet","BLEND_EDGE",EDGE,{"blendedFrom":[makeQuery(id+"F7.boolean.opBoolean","COPY",EDGE,{"derivedFrom":makeQuery(id+"F7.opExtrude","CAP_EDGE",EDGE,{"disambiguationData":[OSD([sQuery(id+"F6.wireOp",EDGE,"E64.2")])],"isStart":false})}),makeQuery(id+"F7.boolean.opBoolean","COPY",EDGE,{"derivedFrom":makeQuery(id+"F7.opExtrude","CAP_EDGE",EDGE,{"disambiguationData":[OSD([sQuery(id+"F6.wireOp",EDGE,"E64.3")])],"isStart":false})})],"blendedInto":[]});
            var Q19;
            Q19=makeQuery(id+"F8.opFillet","BLEND_EDGE",EDGE,{"blendedFrom":[makeQuery(id+"F7.boolean.opBoolean","COPY",EDGE,{"derivedFrom":makeQuery(id+"F7.opExtrude","CAP_EDGE",EDGE,{"disambiguationData":[OSD([sQuery(id+"F6.wireOp",EDGE,"E64.0")])],"isStart":false})}),makeQuery(id+"F7.boolean.opBoolean","COPY",EDGE,{"derivedFrom":makeQuery(id+"F7.opExtrude","CAP_EDGE",EDGE,{"disambiguationData":[OSD([sQuery(id+"F6.wireOp",EDGE,"E64.3")])],"isStart":false})})],"blendedInto":[]});
            fillet(context, id + "F9", {"entities" : qUnion([Q0, Q1, Q2, Q3, Q4, Q5, Q6, Q7, Q8, Q9, Q10, Q11, Q12, Q13, Q14, Q15, Q16, Q17, Q18, Q19]), "radius" : 5.08 * mm, "tangentPropagation" : true, "allowEdgeOverflow" : false});
        }
        {
            var Q0;
            Q0=makeQuery(id+"F3.opExtrude","SWEPT_FACE",FACE,{"disambiguationData":[OSD([sQuery(id+"F2.wireOp",EDGE,"E54")])]});
            cPlane(context, id + "F10", {"entities" : qUnion([Q0]), "cplaneType" : CPlaneType.OFFSET, "offset" : 0 * mm, "width" : 152.4 * mm, "height" : 152.4 * mm});
        }
        {
            var Q0;
            Q0=makeQuery(id+"F3.opExtrude","SWEPT_BODY",BODY,{"disambiguationData":[OSD([sQuery(id+"F2.wireOp",EDGE,"E44.0"),sQuery(id+"F2.wireOp",EDGE,"E45.0"),sQuery(id+"F2.wireOp",EDGE,"E48"),sQuery(id+"F2.wireOp",EDGE,"E49"),sQuery(id+"F2.wireOp",EDGE,"E50"),sQuery(id+"F2.wireOp",EDGE,"E51"),sQuery(id+"F2.wireOp",EDGE,"E52"),sQuery(id+"F2.wireOp",EDGE,"E53.filletArc"),sQuery(id+"F2.wireOp",EDGE,"E54"),sQuery(id+"F2.wireOp",EDGE,"E55"),sQuery(id+"F2.wireOp",EDGE,"E56")])]});
            var Q1;
            Q1=qCreatedBy(id+"F10.planeOp",FACE);
            mirror(context, id + "F11", {"entities" : qUnion([Q0]), "mirrorPlane" : qUnion([Q1])});
        }
        {
            var Q0;
            Q0=makeQuery(id+"F3.opExtrude","SWEPT_BODY",BODY,{"disambiguationData":[OSD([sQuery(id+"F2.wireOp",EDGE,"E44.0"),sQuery(id+"F2.wireOp",EDGE,"E45.0"),sQuery(id+"F2.wireOp",EDGE,"E48"),sQuery(id+"F2.wireOp",EDGE,"E49"),sQuery(id+"F2.wireOp",EDGE,"E50"),sQuery(id+"F2.wireOp",EDGE,"E51"),sQuery(id+"F2.wireOp",EDGE,"E52"),sQuery(id+"F2.wireOp",EDGE,"E53.filletArc"),sQuery(id+"F2.wireOp",EDGE,"E54"),sQuery(id+"F2.wireOp",EDGE,"E55"),sQuery(id+"F2.wireOp",EDGE,"E56")])]});
            var Q1;
            Q1=makeQuery(id+"F11.opPattern","COPY",BODY,{"derivedFrom":makeQuery(id+"F3.opExtrude","SWEPT_BODY",BODY,{"disambiguationData":[OSD([sQuery(id+"F2.wireOp",EDGE,"E44.0"),sQuery(id+"F2.wireOp",EDGE,"E45.0"),sQuery(id+"F2.wireOp",EDGE,"E48"),sQuery(id+"F2.wireOp",EDGE,"E49"),sQuery(id+"F2.wireOp",EDGE,"E50"),sQuery(id+"F2.wireOp",EDGE,"E51"),sQuery(id+"F2.wireOp",EDGE,"E52"),sQuery(id+"F2.wireOp",EDGE,"E53.filletArc"),sQuery(id+"F2.wireOp",EDGE,"E54"),sQuery(id+"F2.wireOp",EDGE,"E55"),sQuery(id+"F2.wireOp",EDGE,"E56")])]}),"instanceName":"1"});
            booleanBodies(context, id + "F12", {"operationType" : BooleanOperationType.UNION, "tools" : qUnion([Q0, Q1])});
        }
    });
